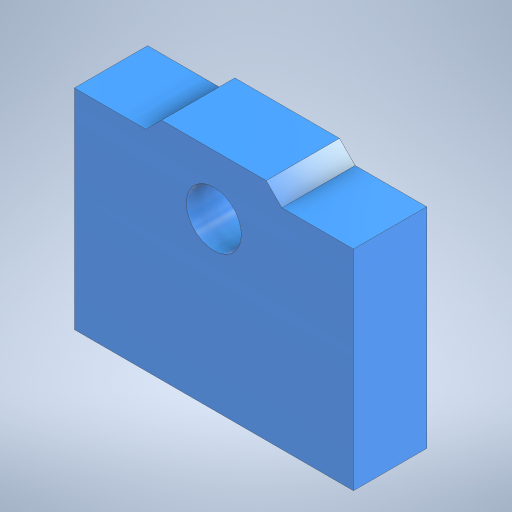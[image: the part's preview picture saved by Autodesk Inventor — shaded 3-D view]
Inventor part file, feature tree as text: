
AUTODESK INVENTOR PART (.ipt)
format: ipt  version: 2024 (Build 280153020, 153B)  size: 336,384 bytes
history: native  units: in
note: dims shown in document units (in); Inventor stores cm internally (conversion verified against a paired STEP export)
features: sketch x9, extrude x8, plane x3, projected_geometry x3, chamfer x1, loft x1
ambient origin geometry x8: Origin, YZ Plane, XZ Plane, XY Plane, X Axis, Y Axis, Z Axis, Center Point
bodies: Solid1 (feature_tree)
feature tree (25):
  extrude  "Extrusion1"  Depth=0.5in
  sketch  "Sketch4"  dims[d2=1.2in d3=0.0in d4=0.95in]
  extrude  "Extrusion2"  Depth=1.2in
  extrude  "Extrusion3"  Depth=0.6in
  chamfer  "Chamfer1"  Distance=1.2in
  extrude  "Extrusion4"  Depth=0.0898in TaperAngle=45.0deg
  plane  "Work Plane1"
  extrude  "Extrusion5"  Depth=0.5in
  sketch  "Sketch7"  dims[d14=0.5in d15=0.5in]
  plane  "Work Plane2"
  loft  "Loft1"
  extrude  "Extrusion6"  [1 undecoded]
  plane  "Work Plane3"
  extrude  "Extrusion7"  Depth=0.0625in
  extrude  "Extrusion8"  TaperAngle=0.0deg  [1 undecoded]
  sketch  "Sketch3"  dims[d0=1.6in d1=0.5in]
  sketch  "Sketch5"  dims[d5=0.315in d6=0.6in d7=1.2in d8=0.0in]
  sketch  "Sketch6"  dims[d9=0.875in d10=0.0in d11=0.0898in d12=0.125in d13=45.0deg]
  projected_geometry  "Projected Loop1"
  sketch  "Sketch8"  dims[d16=0.1299in d17=0.1299in]
  sketch  "Sketch9"  dims[d18=0.7874in d19=0.0in d20=-0.08in]
  projected_geometry  "Projected Loop2"
  sketch  "Sketch10"  dims[d21=0.7874in d22=0.0in d24=0.0625in]
  projected_geometry  "Projected Loop3"
  sketch  "Sketch11"  dims[d25=0.4331in d26=0.0in d27=90.0deg d28=0.0in d29=90.0deg d30=5.0876in d31=0.0in d32=-0.4in d34=0.1112in d35=0.1112in d36=0.1083in d37=0.0in d38=0.3917in d39=0.0in]
note: 2 required parameter values undecoded (feature->parameter linkage not recoverable at this tier; creation-order binding heuristic only, values carry confidence <= 0.55)
